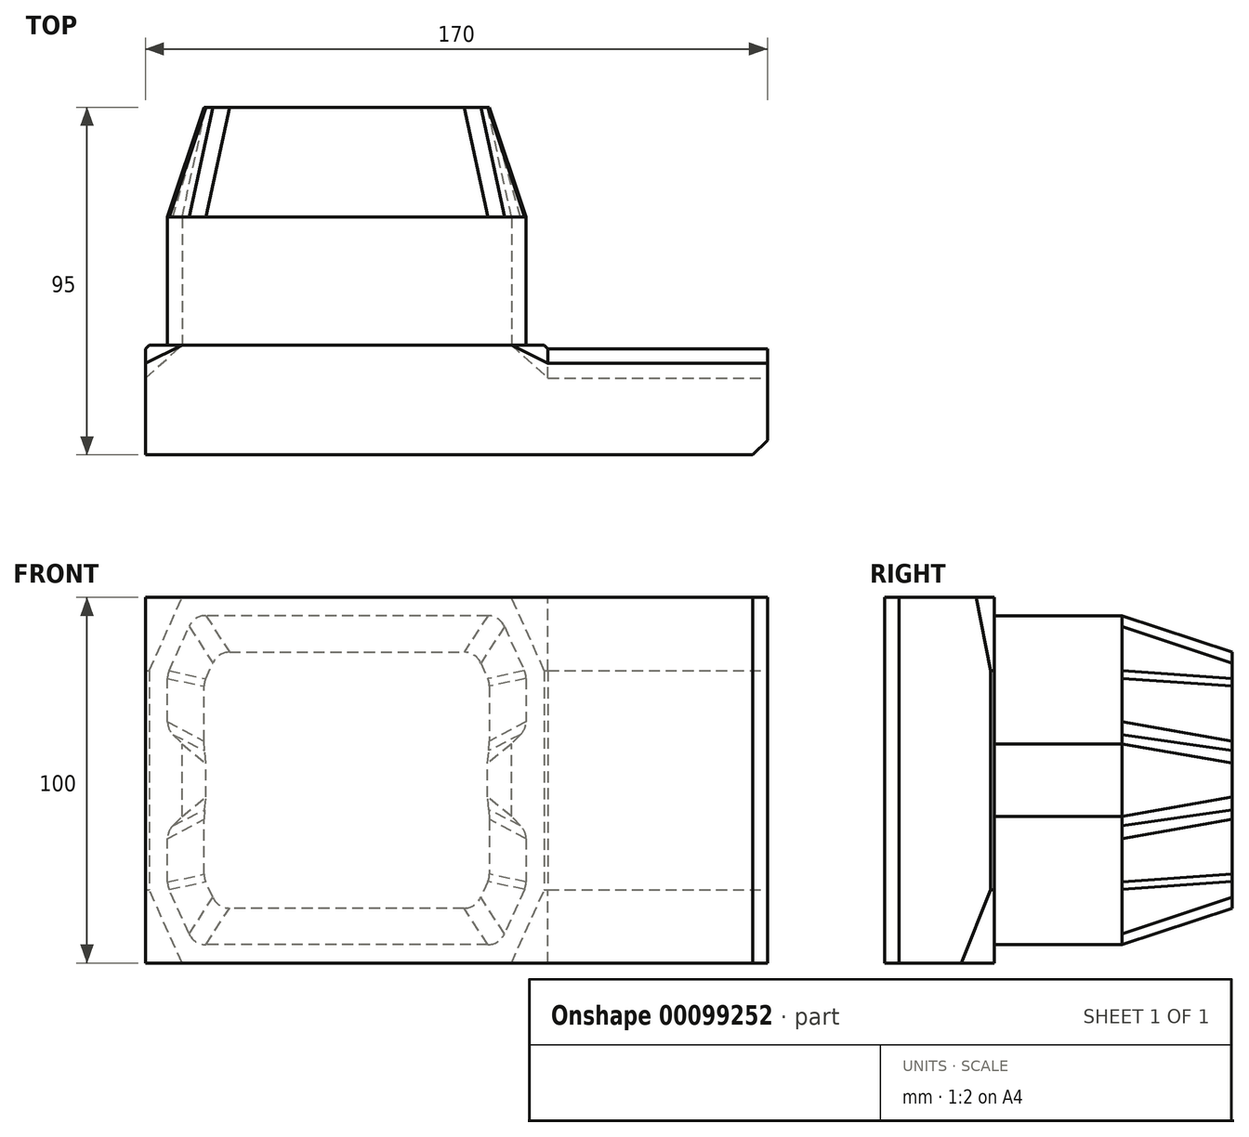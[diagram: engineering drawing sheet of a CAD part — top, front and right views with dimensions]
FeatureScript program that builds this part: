
annotation { "Feature Type Name" : "Feature", "Feature Type Description" : "" }
export const myFeature = defineFeature(function(context is Context, id is Id, definition is map)
    precondition{}
    {
        {
            var Q0;
            Q0=qCreatedBy(makeId("Top.planeOp"),FACE);
            var sketch = newSketch(context, id + "F0", { "sketchPlane" : qUnion([Q0])});
            skLineSegment(sketch, "E0.bottom", {"start": v(0, 0) * mm, "end": v(170, 0) * mm});
            skLineSegment(sketch, "E0.top", {"start": v(0, 85) * mm, "end": v(170, 85) * mm});
            skLineSegment(sketch, "E0.left", {"start": v(0, 0) * mm, "end": v(0, 85) * mm});
            skLineSegment(sketch, "E0.right", {"start": v(170, 0) * mm, "end": v(170, 85) * mm});
            skPoint(sketch, "E1", {"position": v(170, 45) * mm});
            skPoint(sketch, "E2", {"position": v(10, 85) * mm});
            skPoint(sketch, "E3", {"position": v(100, 85) * mm});
            skPoint(sketch, "E4", {"position": v(10, 30) * mm});
            skPoint(sketch, "E5", {"position": v(0, 21) * mm});
            skPoint(sketch, "E6", {"position": v(100, 30) * mm});
            skPoint(sketch, "E7", {"position": v(110, 21) * mm});
            skPoint(sketch, "E8", {"position": v(170, 21) * mm});
            skLineSegment(sketch, "E9", {"start": v(0, 21) * mm, "end": v(10, 30) * mm});
            skLineSegment(sketch, "E10", {"start": v(10, 30) * mm, "end": v(100, 30) * mm});
            skLineSegment(sketch, "E11", {"start": v(100, 30) * mm, "end": v(110, 21) * mm});
            skLineSegment(sketch, "E12", {"start": v(110, 21) * mm, "end": v(170, 21) * mm});
            skPoint(sketch, "E13", {"position": v(170, 0) * mm});
            skPoint(sketch, "E14", {"position": v(166, 0) * mm});
            skPoint(sketch, "E15", {"position": v(170, 4) * mm});
            skLineSegment(sketch, "E16", {"start": v(166, 0) * mm, "end": v(170, 4) * mm});
            skSolve(sketch);
        }
        {
            var Q0;
            {var subQ0=sQuery(id+"F0.wireOp",EDGE,"E9");Q0=makeQuery(id+"F0.imprint","IMPRINT",FACE,{"disambiguationData":[TD([[makeQuery(id+"F0.imprint","IMPRINT",EDGE,{"derivedFrom":subQ0}),-1.0]])]});}
            cPlane(context, id + "F1", {"entities" : qUnion([Q0]), "cplaneType" : CPlaneType.OFFSET, "offset" : 100 * mm, "width" : 150 * mm, "height" : 150 * mm});
        }
        {
            var Q0;
            Q0=qCreatedBy(id+"F1.planeOp",FACE);
            var sketch = newSketch(context, id + "F2", { "sketchPlane" : qUnion([Q0])});
            skLineSegment(sketch, "E17.bottom", {"start": v(0, 0) * mm, "end": v(170, 0) * mm});
            skLineSegment(sketch, "E17.top", {"start": v(0, 85) * mm, "end": v(170, 85) * mm});
            skLineSegment(sketch, "E17.left", {"start": v(0, 0) * mm, "end": v(0, 85) * mm});
            skLineSegment(sketch, "E17.right", {"start": v(170, 0) * mm, "end": v(170, 85) * mm});
            skPoint(sketch, "E18", {"position": v(10, 85) * mm});
            skPoint(sketch, "E19", {"position": v(10, 30) * mm});
            skPoint(sketch, "E20", {"position": v(0, 25) * mm});
            skPoint(sketch, "E21", {"position": v(100, 30) * mm});
            skPoint(sketch, "E22", {"position": v(110, 25) * mm});
            skPoint(sketch, "E23", {"position": v(170, 25) * mm});
            skLineSegment(sketch, "E24", {"start": v(0, 25) * mm, "end": v(10, 30) * mm});
            skLineSegment(sketch, "E25", {"start": v(10, 30) * mm, "end": v(100, 30) * mm});
            skLineSegment(sketch, "E26", {"start": v(100, 30) * mm, "end": v(110, 25) * mm});
            skLineSegment(sketch, "E27", {"start": v(110, 25) * mm, "end": v(170, 25) * mm});
            skPoint(sketch, "E28", {"position": v(170, 0) * mm});
            skPoint(sketch, "E29", {"position": v(166, 0) * mm});
            skPoint(sketch, "E30", {"position": v(170, 4) * mm});
            skLineSegment(sketch, "E31", {"start": v(166, 0) * mm, "end": v(170, 4) * mm});
            skSolve(sketch);
        }
        {
            var Q0;
            {var subQ2=sQuery(id+"F0.wireOp",EDGE,"E0.top");Q0=makeQuery(id+"F0.imprint","IMPRINT",FACE,{"disambiguationData":[TD([[makeQuery(id+"F0.imprint","IMPRINT",EDGE,{"derivedFrom":subQ2}),-1.0]])]});}
            cPlane(context, id + "F3", {"entities" : qUnion([Q0]), "cplaneType" : CPlaneType.OFFSET, "offset" : 20 * mm, "width" : 150 * mm, "height" : 150 * mm});
        }
        {
            var Q0;
            Q0=qCreatedBy(id+"F3.planeOp",FACE);
            var sketch = newSketch(context, id + "F4", { "sketchPlane" : qUnion([Q0])});
            skLineSegment(sketch, "E32.bottom", {"start": v(0, 0) * mm, "end": v(170, 0) * mm});
            skLineSegment(sketch, "E32.top", {"start": v(0, 85) * mm, "end": v(170, 85) * mm});
            skLineSegment(sketch, "E32.left", {"start": v(0, 0) * mm, "end": v(0, 85) * mm});
            skLineSegment(sketch, "E32.right", {"start": v(170, 0) * mm, "end": v(170, 85) * mm});
            skPoint(sketch, "E33", {"position": v(10, 85) * mm});
            skPoint(sketch, "E34", {"position": v(1, 30) * mm});
            skPoint(sketch, "E35", {"position": v(0, 29) * mm});
            skPoint(sketch, "E36", {"position": v(109, 30) * mm});
            skPoint(sketch, "E37", {"position": v(110, 29) * mm});
            skPoint(sketch, "E38", {"position": v(170, 29) * mm});
            skLineSegment(sketch, "E39", {"start": v(0, 29) * mm, "end": v(1, 30) * mm});
            skLineSegment(sketch, "E40", {"start": v(1, 30) * mm, "end": v(109, 30) * mm});
            skLineSegment(sketch, "E41", {"start": v(109, 30) * mm, "end": v(110, 29) * mm});
            skLineSegment(sketch, "E42", {"start": v(110, 29) * mm, "end": v(170, 29) * mm});
            skPoint(sketch, "E43", {"position": v(170, 0) * mm});
            skPoint(sketch, "E44", {"position": v(166, 0) * mm});
            skPoint(sketch, "E45", {"position": v(170, 4) * mm});
            skLineSegment(sketch, "E46", {"start": v(166, 0) * mm, "end": v(170, 4) * mm});
            skSolve(sketch);
        }
        {
            var Q0;
            {var subQ0=sQuery(id+"F0.wireOp",EDGE,"E9");Q0=makeQuery(id+"F0.imprint","IMPRINT",FACE,{"disambiguationData":[TD([[makeQuery(id+"F0.imprint","IMPRINT",EDGE,{"derivedFrom":subQ0}),-1.0]])]});}
            var Q1;
            {var subQ0=sQuery(id+"F4.wireOp",EDGE,"E39");Q1=makeQuery(id+"F4.imprint","IMPRINT",FACE,{"disambiguationData":[TD([[makeQuery(id+"F4.imprint","IMPRINT",EDGE,{"derivedFrom":subQ0}),-1.0]])]});}
            loft(context, id + "F5", {"sheetProfilesArray" : [{ "sheetProfileEntities" : qUnion([Q0]) }, { "sheetProfileEntities" : qUnion([Q1]) }]});
        }
        {
            var Q0;
            {var subQ1=sQuery(id+"F2.wireOp",EDGE,"E17.top");Q0=makeQuery(id+"F2.imprint","IMPRINT",FACE,{"disambiguationData":[TD([[makeQuery(id+"F2.imprint","IMPRINT",EDGE,{"derivedFrom":subQ1}),-1.0]])]});}
            cPlane(context, id + "F6", {"entities" : qUnion([Q0]), "cplaneType" : CPlaneType.OFFSET, "offset" : 20 * mm, "oppositeDirection" : true, "width" : 150 * mm, "height" : 150 * mm});
        }
        {
            var Q0;
            Q0=qCreatedBy(id+"F6.planeOp",FACE);
            var sketch = newSketch(context, id + "F7", { "sketchPlane" : qUnion([Q0])});
            skLineSegment(sketch, "E47.bottom", {"start": v(0, 0) * mm, "end": v(170, 0) * mm});
            skLineSegment(sketch, "E47.top", {"start": v(0, 85) * mm, "end": v(170, 85) * mm});
            skLineSegment(sketch, "E47.left", {"start": v(0, 0) * mm, "end": v(0, 85) * mm});
            skLineSegment(sketch, "E47.right", {"start": v(170, 0) * mm, "end": v(170, 85) * mm});
            skPoint(sketch, "E48", {"position": v(10, 85) * mm});
            skPoint(sketch, "E49", {"position": v(1, 30) * mm});
            skPoint(sketch, "E50", {"position": v(0, 29) * mm});
            skPoint(sketch, "E51", {"position": v(109, 30) * mm});
            skPoint(sketch, "E52", {"position": v(110, 29) * mm});
            skPoint(sketch, "E53", {"position": v(170, 29) * mm});
            skLineSegment(sketch, "E54", {"start": v(0, 29) * mm, "end": v(1, 30) * mm});
            skLineSegment(sketch, "E55", {"start": v(1, 30) * mm, "end": v(109, 30) * mm});
            skLineSegment(sketch, "E56", {"start": v(109, 30) * mm, "end": v(110, 29) * mm});
            skLineSegment(sketch, "E57", {"start": v(110, 29) * mm, "end": v(170, 29) * mm});
            skPoint(sketch, "E58", {"position": v(170, 0) * mm});
            skPoint(sketch, "E59", {"position": v(166, 0) * mm});
            skPoint(sketch, "E60", {"position": v(170, 4) * mm});
            skLineSegment(sketch, "E61", {"start": v(166, 0) * mm, "end": v(170, 4) * mm});
            skSolve(sketch);
        }
        {
            var Q0;
            {var subQ0=sQuery(id+"F7.wireOp",EDGE,"E54");Q0=makeQuery(id+"F7.imprint","IMPRINT",FACE,{"disambiguationData":[TD([[makeQuery(id+"F7.imprint","IMPRINT",EDGE,{"derivedFrom":subQ0}),-1.0]])]});}
            var Q1;
            {var subQ3=sQuery(id+"F2.wireOp",EDGE,"E24");Q1=makeQuery(id+"F2.imprint","IMPRINT",FACE,{"disambiguationData":[TD([[makeQuery(id+"F2.imprint","IMPRINT",EDGE,{"derivedFrom":subQ3}),-1.0]])]});}
            loft(context, id + "F8", {"sheetProfilesArray" : [{ "sheetProfileEntities" : qUnion([Q0]) }, { "sheetProfileEntities" : qUnion([Q1]) }]});
        }
        {
            var Q0;
            {var subQ0=sQuery(id+"F4.wireOp",EDGE,"E39");Q0=makeQuery(id+"F5.opLoft","CAP_FACE",FACE,{"disambiguationData":[OSD([makeQuery(id+"F4.imprint","IMPRINT",FACE,{"disambiguationData":[TD([[makeQuery(id+"F4.imprint","IMPRINT",EDGE,{"derivedFrom":subQ0}),-1.0]])]})])],"isStart":true});}
            var Q1;
            {var subQ0=sQuery(id+"F7.wireOp",EDGE,"E54");Q1=makeQuery(id+"F8.opLoft","CAP_FACE",FACE,{"disambiguationData":[OSD([makeQuery(id+"F7.imprint","IMPRINT",FACE,{"disambiguationData":[TD([[makeQuery(id+"F7.imprint","IMPRINT",EDGE,{"derivedFrom":subQ0}),-1.0]])]})])],"isStart":true});}
            extrude(context, id + "F9", {"entities" : qUnion([Q0]), "endBound" : BoundingType.UP_TO_SURFACE, "endBoundEntityFace" : qUnion([Q1]), "depth" : 50 * mm});
        }
        {
            var Q0;
            {var subQ0=sQuery(id+"F4.wireOp",EDGE,"E39");var subQ7=sQuery(id+"F0.wireOp",EDGE,"E9");Q0=makeQuery(id+"F5.opLoft","SWEPT_BODY",BODY,{"disambiguationData":[OSD([makeQuery(id+"F0.imprint","IMPRINT",FACE,{"disambiguationData":[TD([[makeQuery(id+"F0.imprint","IMPRINT",EDGE,{"derivedFrom":subQ7}),-1.0]])]}),makeQuery(id+"F4.imprint","IMPRINT",FACE,{"disambiguationData":[TD([[makeQuery(id+"F4.imprint","IMPRINT",EDGE,{"derivedFrom":subQ0}),-1.0]])]})])]});}
            var Q1;
            {var subQ0=sQuery(id+"F4.wireOp",EDGE,"E39");Q1=makeQuery(id+"F9.opExtrude","SWEPT_BODY",BODY,{"disambiguationData":[OSD([makeQuery(id+"F4.imprint","IMPRINT",FACE,{"disambiguationData":[TD([[makeQuery(id+"F4.imprint","IMPRINT",EDGE,{"derivedFrom":subQ0}),-1.0]])]})])]});}
            var Q2;
            {var subQ0=sQuery(id+"F7.wireOp",EDGE,"E54");var subQ10=sQuery(id+"F2.wireOp",EDGE,"E24");Q2=makeQuery(id+"F8.opLoft","SWEPT_BODY",BODY,{"disambiguationData":[OSD([makeQuery(id+"F2.imprint","IMPRINT",FACE,{"disambiguationData":[TD([[makeQuery(id+"F2.imprint","IMPRINT",EDGE,{"derivedFrom":subQ10}),-1.0]])]}),makeQuery(id+"F7.imprint","IMPRINT",FACE,{"disambiguationData":[TD([[makeQuery(id+"F7.imprint","IMPRINT",EDGE,{"derivedFrom":subQ0}),-1.0]])]})])]});}
            booleanBodies(context, id + "F10", {"operationType" : BooleanOperationType.UNION, "tools" : qUnion([Q0, Q1, Q2])});
        }
        {
            var Q0;
            {var subQ0=sQuery(id+"F4.wireOp",EDGE,"E41");var subQ1=sQuery(id+"F4.wireOp",EDGE,"E40");var subQ2=sQuery(id+"F4.wireOp",EDGE,"E39");Q0=makeQuery(id+"F10.opBoolean","MERGE",FACE,{"derivedFrom":[makeQuery(id+"F5.opLoft","SWEPT_FACE",FACE,{"disambiguationData":[OSD([sQuery(id+"F0.wireOp",EDGE,"E9"),sQuery(id+"F0.wireOp",EDGE,"E10"),sQuery(id+"F0.wireOp",EDGE,"E11"),subQ2,subQ1,subQ0])]}),makeQuery(id+"F8.opLoft","SWEPT_FACE",FACE,{"disambiguationData":[OSD([sQuery(id+"F2.wireOp",EDGE,"E24"),sQuery(id+"F2.wireOp",EDGE,"E25"),sQuery(id+"F2.wireOp",EDGE,"E26"),sQuery(id+"F7.wireOp",EDGE,"E54"),sQuery(id+"F7.wireOp",EDGE,"E55"),sQuery(id+"F7.wireOp",EDGE,"E56")])]}),makeQuery(id+"F9.opExtrude","SWEPT_FACE",FACE,{"disambiguationData":[OSD([subQ2,subQ1,subQ0])]})]});}
            var sketch = newSketch(context, id + "F11", { "sketchPlane" : qUnion([Q0])});
            skLineSegment(sketch, "E62.0", {"start": v(-93.53, 5) * mm, "end": v(-16.47, 5) * mm});
            skLineSegment(sketch, "E62.1", {"start": v(-103.56, 20.1) * mm, "end": v(-98.1, 7.95) * mm});
            skLineSegment(sketch, "E62.2", {"start": v(-11.9, 7.95) * mm, "end": v(-6.44, 20.1) * mm});
            skLineSegment(sketch, "E62.3", {"start": v(-104, 77.85) * mm, "end": v(-104, 66) * mm});
            skLineSegment(sketch, "E62.4", {"start": v(-6, 22.15) * mm, "end": v(-6, 34) * mm});
            skLineSegment(sketch, "E62.5", {"start": v(-6.44, 79.9) * mm, "end": v(-11.9, 92.05) * mm});
            skLineSegment(sketch, "E62.6", {"start": v(-93.53, 95) * mm, "end": v(-16.47, 95) * mm});
            skLineSegment(sketch, "E62.7", {"start": v(-98.1, 92.05) * mm, "end": v(-103.56, 79.9) * mm});
            skPoint(sketch, "E63", {"position": v(-6, 36.07) * mm});
            skLineSegment(sketch, "E64", {"start": v(-7.46, 37.54) * mm, "end": v(-10, 40.07) * mm});
            skLineSegment(sketch, "E65.MirrorCS", {"start": v(-7.46, 62.46) * mm, "end": v(-10, 59.93) * mm});
            skLineSegment(sketch, "E66.trimOffspring", {"start": v(-6, 66) * mm, "end": v(-6, 77.85) * mm});
            skLineSegment(sketch, "E67", {"start": v(-10, 40.07) * mm, "end": v(-10, 59.93) * mm});
            skLineSegment(sketch, "E68.MirrorCS", {"start": v(-102.54, 62.46) * mm, "end": v(-100, 59.93) * mm});
            skLineSegment(sketch, "E69.MirrorCS", {"start": v(-100, 40.07) * mm, "end": v(-100, 59.93) * mm});
            skLineSegment(sketch, "E70.MirrorCS", {"start": v(-102.54, 37.54) * mm, "end": v(-100, 40.07) * mm});
            skLineSegment(sketch, "E71.trimOffspring", {"start": v(-104, 34) * mm, "end": v(-104, 22.15) * mm});
            skPoint(sketch, "E72.visualSharp", {"position": v(-13.23, 5) * mm});
            skArc(sketch, "E72.filletArc", {"start": v(-16.47, 5) * mm, "mid": v(-13.75, 5.8) * mm, "end": v(-11.9, 7.95) * mm});
            skPoint(sketch, "E73.visualSharp", {"position": v(-6, 21.07) * mm});
            skArc(sketch, "E73.filletArc", {"start": v(-6.44, 20.1) * mm, "mid": v(-6.11, 21.1) * mm, "end": v(-6, 22.15) * mm});
            skArc(sketch, "E74.filletArc", {"start": v(-6, 34) * mm, "mid": v(-6.38, 35.92) * mm, "end": v(-7.46, 37.54) * mm});
            skPoint(sketch, "E75.visualSharp", {"position": v(-6, 63.93) * mm});
            skArc(sketch, "E75.filletArc", {"start": v(-7.46, 62.46) * mm, "mid": v(-6.38, 64.08) * mm, "end": v(-6, 66) * mm});
            skPoint(sketch, "E76.visualSharp", {"position": v(-6, 78.93) * mm});
            skArc(sketch, "E76.filletArc", {"start": v(-6, 77.85) * mm, "mid": v(-6.11, 78.9) * mm, "end": v(-6.44, 79.9) * mm});
            skPoint(sketch, "E77.visualSharp", {"position": v(-13.23, 95) * mm});
            skArc(sketch, "E77.filletArc", {"start": v(-11.9, 92.05) * mm, "mid": v(-13.75, 94.2) * mm, "end": v(-16.47, 95) * mm});
            skPoint(sketch, "E78.visualSharp", {"position": v(-96.77, 95) * mm});
            skArc(sketch, "E78.filletArc", {"start": v(-93.53, 95) * mm, "mid": v(-96.25, 94.2) * mm, "end": v(-98.1, 92.05) * mm});
            skPoint(sketch, "E79.visualSharp", {"position": v(-104, 78.93) * mm});
            skArc(sketch, "E79.filletArc", {"start": v(-103.56, 79.9) * mm, "mid": v(-103.89, 78.9) * mm, "end": v(-104, 77.85) * mm});
            skPoint(sketch, "E80.visualSharp", {"position": v(-104, 63.93) * mm});
            skArc(sketch, "E80.filletArc", {"start": v(-104, 66) * mm, "mid": v(-103.62, 64.08) * mm, "end": v(-102.54, 62.46) * mm});
            skPoint(sketch, "E81.visualSharp", {"position": v(-104, 36.07) * mm});
            skArc(sketch, "E81.filletArc", {"start": v(-102.54, 37.54) * mm, "mid": v(-103.62, 35.92) * mm, "end": v(-104, 34) * mm});
            skPoint(sketch, "E82.visualSharp", {"position": v(-104, 21.07) * mm});
            skArc(sketch, "E82.filletArc", {"start": v(-104, 22.15) * mm, "mid": v(-103.89, 21.1) * mm, "end": v(-103.56, 20.1) * mm});
            skPoint(sketch, "E83.visualSharp", {"position": v(-96.77, 5) * mm});
            skArc(sketch, "E83.filletArc", {"start": v(-98.1, 7.95) * mm, "mid": v(-96.25, 5.8) * mm, "end": v(-93.53, 5) * mm});
            skSolve(sketch);
        }
        {
            var Q0;
            Q0=makeQuery(id+"F11.imprint","IMPRINT",FACE,{"disambiguationData":[TD([[makeQuery(id+"F11.imprint","IMPRINT",EDGE,{"derivedFrom":sQuery(id+"F11.wireOp",EDGE,"E62.0")}),1.0]])]});
            extrude(context, id + "F12", {"entities" : qUnion([Q0]), "operationType" : NewBodyOperationType.ADD, "depth" : 35 * mm});
        }
        {
            var Q0;
            Q0=makeQuery(id+"F12.opExtrude","CAP_FACE",FACE,{"disambiguationData":[OSD([sQuery(id+"F11.wireOp",EDGE,"E62.0"),sQuery(id+"F11.wireOp",EDGE,"E62.1"),sQuery(id+"F11.wireOp",EDGE,"E62.2"),sQuery(id+"F11.wireOp",EDGE,"E62.3"),sQuery(id+"F11.wireOp",EDGE,"E62.4"),sQuery(id+"F11.wireOp",EDGE,"E62.5"),sQuery(id+"F11.wireOp",EDGE,"E62.6"),sQuery(id+"F11.wireOp",EDGE,"E62.7"),sQuery(id+"F11.wireOp",EDGE,"E64"),sQuery(id+"F11.wireOp",EDGE,"E65.MirrorCS"),sQuery(id+"F11.wireOp",EDGE,"E66.trimOffspring"),sQuery(id+"F11.wireOp",EDGE,"E67"),sQuery(id+"F11.wireOp",EDGE,"E68.MirrorCS"),sQuery(id+"F11.wireOp",EDGE,"E69.MirrorCS"),sQuery(id+"F11.wireOp",EDGE,"E70.MirrorCS"),sQuery(id+"F11.wireOp",EDGE,"E71.trimOffspring")])],"isStart":false});
            cPlane(context, id + "F13", {"entities" : qUnion([Q0]), "cplaneType" : CPlaneType.OFFSET, "offset" : 30 * mm, "width" : 150 * mm, "height" : 150 * mm});
        }
        {
            var Q0;
            Q0=qCreatedBy(id+"F13.planeOp",FACE);
            var sketch = newSketch(context, id + "F14", { "sketchPlane" : qUnion([Q0])});
            skLineSegment(sketch, "E84.0", {"start": v(-16.44, 77.76) * mm, "end": v(-18.37, 82.05) * mm});
            skLineSegment(sketch, "E84.1", {"start": v(-16, 60.7) * mm, "end": v(-16, 75.7) * mm});
            skLineSegment(sketch, "E84.2", {"start": v(-16.5, 54.64) * mm, "end": v(-16.13, 58.11) * mm});
            skLineSegment(sketch, "E84.3", {"start": v(-16.5, 45.36) * mm, "end": v(-16.5, 54.64) * mm});
            skLineSegment(sketch, "E84.4", {"start": v(-16.13, 41.89) * mm, "end": v(-16.5, 45.36) * mm});
            skLineSegment(sketch, "E84.7", {"start": v(-94, 75.7) * mm, "end": v(-94, 60.7) * mm});
            skLineSegment(sketch, "E84.8", {"start": v(-91.63, 82.05) * mm, "end": v(-93.56, 77.76) * mm});
            skLineSegment(sketch, "E84.10", {"start": v(-94, 39.3) * mm, "end": v(-94, 24.3) * mm});
            skLineSegment(sketch, "E84.11", {"start": v(-93.56, 22.24) * mm, "end": v(-91.63, 17.95) * mm});
            skLineSegment(sketch, "E84.12", {"start": v(-87.07, 15) * mm, "end": v(-22.93, 15) * mm});
            skLineSegment(sketch, "E84.13", {"start": v(-18.37, 17.95) * mm, "end": v(-16.44, 22.24) * mm});
            skLineSegment(sketch, "E84.14", {"start": v(-22.93, 85) * mm, "end": v(-87.07, 85) * mm});
            skLineSegment(sketch, "E84.15", {"start": v(-16, 24.3) * mm, "end": v(-16, 39.3) * mm});
            skPoint(sketch, "E85.visualSharp", {"position": v(-90.3, 85) * mm});
            skArc(sketch, "E85.filletArc", {"start": v(-87.07, 85) * mm, "mid": v(-89.78, 84.2) * mm, "end": v(-91.63, 82.05) * mm});
            skPoint(sketch, "E86.visualSharp", {"position": v(-94, 76.78) * mm});
            skArc(sketch, "E86.filletArc", {"start": v(-93.56, 77.76) * mm, "mid": v(-93.89, 76.76) * mm, "end": v(-94, 75.7) * mm});
            skPoint(sketch, "E87.visualSharp", {"position": v(-94, 23.22) * mm});
            skArc(sketch, "E87.filletArc", {"start": v(-94, 24.3) * mm, "mid": v(-93.89, 23.24) * mm, "end": v(-93.56, 22.24) * mm});
            skPoint(sketch, "E88.visualSharp", {"position": v(-90.3, 15) * mm});
            skArc(sketch, "E88.filletArc", {"start": v(-91.63, 17.95) * mm, "mid": v(-89.78, 15.8) * mm, "end": v(-87.07, 15) * mm});
            skPoint(sketch, "E89.visualSharp", {"position": v(-19.7, 15) * mm});
            skArc(sketch, "E89.filletArc", {"start": v(-22.93, 15) * mm, "mid": v(-20.22, 15.8) * mm, "end": v(-18.37, 17.95) * mm});
            skPoint(sketch, "E90.visualSharp", {"position": v(-16, 23.22) * mm});
            skArc(sketch, "E90.filletArc", {"start": v(-16.44, 22.24) * mm, "mid": v(-16.11, 23.24) * mm, "end": v(-16, 24.3) * mm});
            skPoint(sketch, "E91.visualSharp", {"position": v(-16, 76.78) * mm});
            skArc(sketch, "E91.filletArc", {"start": v(-16, 75.7) * mm, "mid": v(-16.11, 76.76) * mm, "end": v(-16.44, 77.76) * mm});
            skPoint(sketch, "E92.visualSharp", {"position": v(-19.7, 85) * mm});
            skArc(sketch, "E92.filletArc", {"start": v(-18.37, 82.05) * mm, "mid": v(-20.22, 84.2) * mm, "end": v(-22.93, 85) * mm});
            skLineSegment(sketch, "E93", {"start": v(-16.13, 41.89) * mm, "end": v(-16, 39.3) * mm});
            skLineSegment(sketch, "E94", {"start": v(-16.13, 58.11) * mm, "end": v(-16, 60.7) * mm});
            skLineSegment(sketch, "E95.MirrorCS", {"start": v(-93.87, 41.89) * mm, "end": v(-94, 39.3) * mm});
            skLineSegment(sketch, "E96.MirrorCS", {"start": v(-93.87, 41.89) * mm, "end": v(-93.5, 45.36) * mm});
            skLineSegment(sketch, "E97.MirrorCS", {"start": v(-93.5, 45.36) * mm, "end": v(-93.5, 54.64) * mm});
            skLineSegment(sketch, "E98.MirrorCS", {"start": v(-93.5, 54.64) * mm, "end": v(-93.87, 58.11) * mm});
            skLineSegment(sketch, "E99.MirrorCS", {"start": v(-93.87, 58.11) * mm, "end": v(-94, 60.7) * mm});
            skSolve(sketch);
        }
        {
            var Q1;
            Q1=makeQuery(id+"F12.opExtrude","CAP_FACE",FACE,{"disambiguationData":[OSD([sQuery(id+"F11.wireOp",EDGE,"E62.0"),sQuery(id+"F11.wireOp",EDGE,"E62.1"),sQuery(id+"F11.wireOp",EDGE,"E62.2"),sQuery(id+"F11.wireOp",EDGE,"E62.3"),sQuery(id+"F11.wireOp",EDGE,"E62.4"),sQuery(id+"F11.wireOp",EDGE,"E62.5"),sQuery(id+"F11.wireOp",EDGE,"E62.6"),sQuery(id+"F11.wireOp",EDGE,"E62.7"),sQuery(id+"F11.wireOp",EDGE,"E64"),sQuery(id+"F11.wireOp",EDGE,"E65.MirrorCS"),sQuery(id+"F11.wireOp",EDGE,"E66.trimOffspring"),sQuery(id+"F11.wireOp",EDGE,"E67"),sQuery(id+"F11.wireOp",EDGE,"E68.MirrorCS"),sQuery(id+"F11.wireOp",EDGE,"E69.MirrorCS"),sQuery(id+"F11.wireOp",EDGE,"E70.MirrorCS"),sQuery(id+"F11.wireOp",EDGE,"E71.trimOffspring"),sQuery(id+"F11.wireOp",EDGE,"E72.filletArc"),sQuery(id+"F11.wireOp",EDGE,"E73.filletArc"),sQuery(id+"F11.wireOp",EDGE,"E74.filletArc"),sQuery(id+"F11.wireOp",EDGE,"E75.filletArc"),sQuery(id+"F11.wireOp",EDGE,"E76.filletArc"),sQuery(id+"F11.wireOp",EDGE,"E77.filletArc"),sQuery(id+"F11.wireOp",EDGE,"E78.filletArc"),sQuery(id+"F11.wireOp",EDGE,"E79.filletArc"),sQuery(id+"F11.wireOp",EDGE,"E80.filletArc"),sQuery(id+"F11.wireOp",EDGE,"E81.filletArc"),sQuery(id+"F11.wireOp",EDGE,"E82.filletArc"),sQuery(id+"F11.wireOp",EDGE,"E83.filletArc")])],"isStart":false});
            var Q2;
            Q2=makeQuery(id+"F14.imprint","IMPRINT",FACE,{"disambiguationData":[TD([[makeQuery(id+"F14.imprint","IMPRINT",EDGE,{"derivedFrom":sQuery(id+"F14.wireOp",EDGE,"E84.0")}),1.0]])]});
            loft(context, id + "F15", {"operationType" : NewBodyOperationType.ADD, "sheetProfilesArray" : [{ "sheetProfileEntities" : qUnion([Q1]) }, { "sheetProfileEntities" : qUnion([Q2]) }]});
        }
    });
